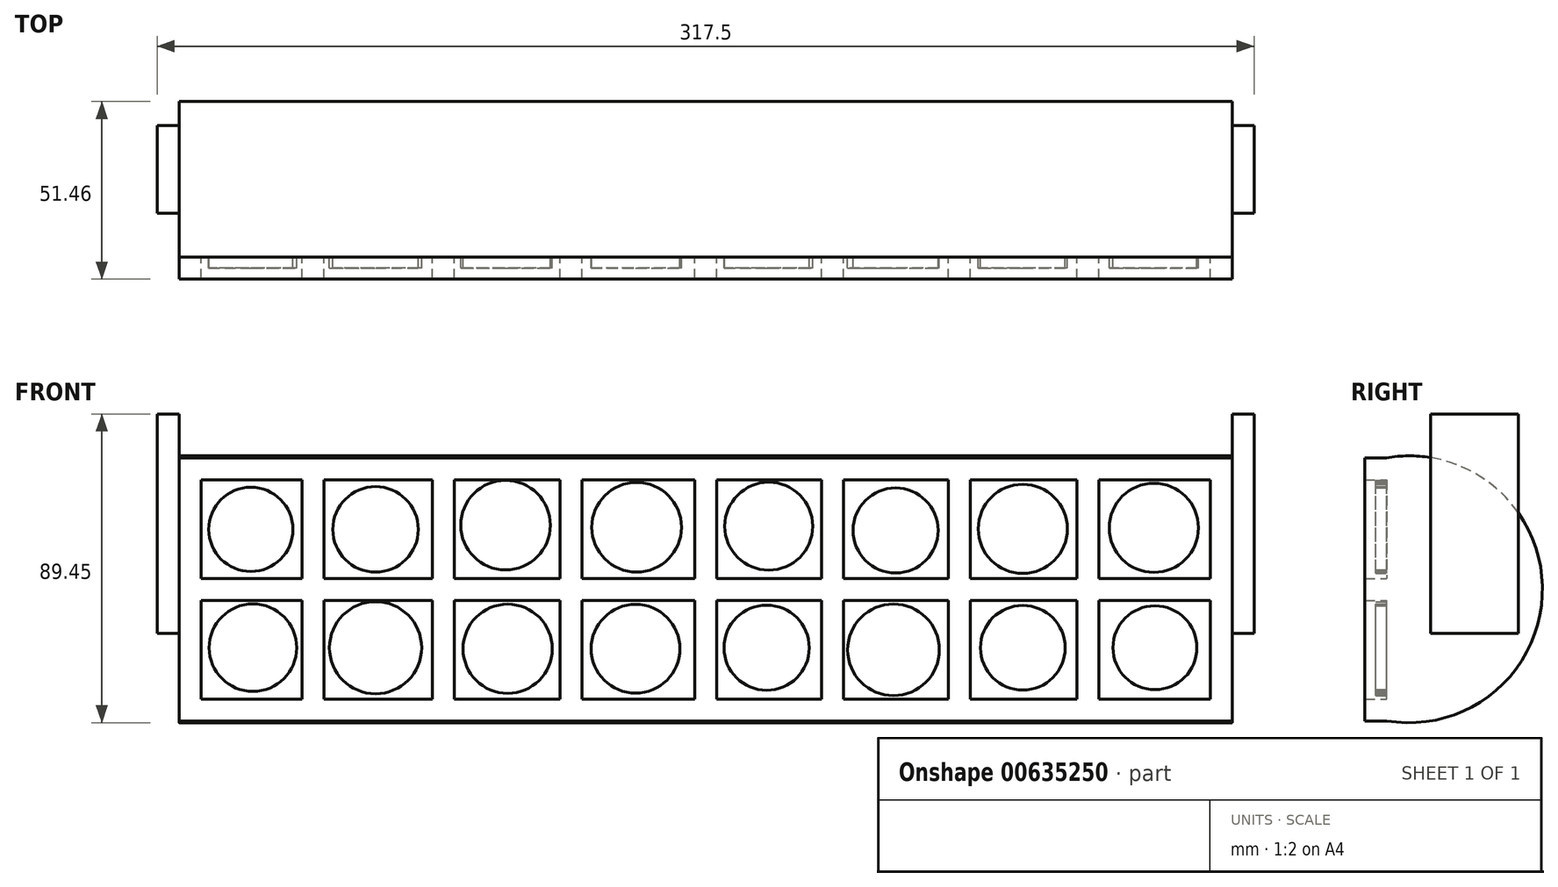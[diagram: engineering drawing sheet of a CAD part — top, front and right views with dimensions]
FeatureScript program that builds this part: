
annotation { "Feature Type Name" : "Feature", "Feature Type Description" : "" }
export const myFeature = defineFeature(function(context is Context, id is Id, definition is map)
    precondition{}
    {
        {
            var Q0;
            Q0=qCreatedBy(makeId("Right.planeOp"),FACE);
            var sketch = newSketch(context, id + "F0", { "sketchPlane" : qUnion([Q0])});
            skLineSegment(sketch, "E0", {"start": v(0, 0) * mm, "end": v(0, 76.2) * mm});
            skArc(sketch, "E1", {"start": v(0, 0) * mm, "mid": v(45.11, 38.1) * mm, "end": v(0, 76.2) * mm});
            skSolve(sketch);
        }
        {
            var Q0;
            Q0 = qSketchRegion(id + "F0", true);
            extrude(context, id + "F1", {"entities" : qUnion([Q0]), "depth" : 304.8 * mm, "offsetDistance" : 25.4 * mm});
        }
        {
            var Q0;
            Q0=makeQuery(id+"F1.opExtrude","CAP_FACE",FACE,{"disambiguationData":[OSD([sQuery(id+"F0.wireOp",EDGE,"E0"),sQuery(id+"F0.wireOp",EDGE,"E1")])],"isStart":true});
            var sketch = newSketch(context, id + "F2", { "sketchPlane" : qUnion([Q0])});
            skLineSegment(sketch, "E2.bottom", {"start": v(-38.1, 25.4) * mm, "end": v(-12.7, 25.4) * mm});
            skLineSegment(sketch, "E2.top", {"start": v(-38.1, 88.9) * mm, "end": v(-12.7, 88.9) * mm});
            skLineSegment(sketch, "E2.left", {"start": v(-38.1, 25.4) * mm, "end": v(-38.1, 88.9) * mm});
            skLineSegment(sketch, "E2.right", {"start": v(-12.7, 25.4) * mm, "end": v(-12.7, 88.9) * mm});
            skSolve(sketch);
        }
        {
            var Q0;
            Q0 = qSketchRegion(id + "F2", true);
            extrude(context, id + "F3", {"entities" : qUnion([Q0]), "operationType" : NewBodyOperationType.ADD, "depth" : 6.35 * mm, "offsetDistance" : 25.4 * mm});
        }
        {
            var Q0;
            Q0=makeQuery(id+"F1.opExtrude","CAP_FACE",FACE,{"disambiguationData":[OSD([sQuery(id+"F0.wireOp",EDGE,"E0"),sQuery(id+"F0.wireOp",EDGE,"E1")])],"isStart":false});
            var sketch = newSketch(context, id + "F4", { "sketchPlane" : qUnion([Q0])});
            skLineSegment(sketch, "E3.bottom", {"start": v(12.7, 25.4) * mm, "end": v(38.1, 25.4) * mm});
            skLineSegment(sketch, "E3.top", {"start": v(12.7, 88.9) * mm, "end": v(38.1, 88.9) * mm});
            skLineSegment(sketch, "E3.left", {"start": v(12.7, 25.4) * mm, "end": v(12.7, 88.9) * mm});
            skLineSegment(sketch, "E3.right", {"start": v(38.1, 25.4) * mm, "end": v(38.1, 88.9) * mm});
            skSolve(sketch);
        }
        {
            var Q0;
            Q0 = qSketchRegion(id + "F4", true);
            extrude(context, id + "F5", {"entities" : qUnion([Q0]), "operationType" : NewBodyOperationType.ADD, "depth" : 6.35 * mm, "offsetDistance" : 25.4 * mm});
        }
        {
            var Q0;
            Q0=makeQuery(id+"F1.opExtrude","SWEPT_FACE",FACE,{"disambiguationData":[OSD([sQuery(id+"F0.wireOp",EDGE,"E0")])]});
            var sketch = newSketch(context, id + "F6", { "sketchPlane" : qUnion([Q0])});
            skLineSegment(sketch, "E4.0", {"start": v(298.45, 69.85) * mm, "end": v(6.35, 69.85) * mm});
            skLineSegment(sketch, "E4.1", {"start": v(298.45, 6.35) * mm, "end": v(298.45, 69.85) * mm});
            skLineSegment(sketch, "E4.2", {"start": v(298.45, 6.35) * mm, "end": v(6.35, 6.35) * mm});
            skLineSegment(sketch, "E4.3", {"start": v(6.35, 6.35) * mm, "end": v(6.35, 69.85) * mm});
            skSolve(sketch);
        }
        {
            var Q0;
            Q0=makeQuery(id+"F6.imprint","IMPRINT",FACE,{"disambiguationData":[TD([[makeQuery(id+"F6.imprint","IMPRINT",EDGE,{"derivedFrom":sQuery(id+"F6.wireOp",EDGE,"E4.0")}),-1.0]])]});
            extrude(context, id + "F7", {"entities" : qUnion([Q0]), "operationType" : NewBodyOperationType.ADD, "depth" : 6.35 * mm, "offsetDistance" : 25.4 * mm});
        }
        {
            var Q0;
            Q0=makeQuery(id+"F1.opExtrude","SWEPT_FACE",FACE,{"disambiguationData":[OSD([sQuery(id+"F0.wireOp",EDGE,"E0")])]});
            var sketch = newSketch(context, id + "F8", { "sketchPlane" : qUnion([Q0])});
            skLineSegment(sketch, "E5.top", {"start": v(298.45, 41.27) * mm, "end": v(266.24, 41.27) * mm});
            skLineSegment(sketch, "E5.left", {"start": v(298.45, 34.92) * mm, "end": v(298.45, 41.27) * mm});
            skLineSegment(sketch, "E5.right", {"start": v(6.35, 34.92) * mm, "end": v(6.35, 41.27) * mm});
            skPoint(sketch, "E5.middle", {"position": v(152.4, 38.1) * mm});
            skPoint(sketch, "E5.middle.positionSnap0", {"position": v(6.35, 38.1) * mm});
            skPoint(sketch, "E5.middle.positionSnap1", {"position": v(152.4, 6.35) * mm});
            skPoint(sketch, "E5.centerSnap0", {"position": v(6.35, 38.1) * mm});
            skPoint(sketch, "E5.centerSnap1", {"position": v(152.4, 6.35) * mm});
            skLineSegment(sketch, "E6.bottom", {"start": v(149.23, 69.85) * mm, "end": v(155.58, 69.85) * mm});
            skLineSegment(sketch, "E6.top", {"start": v(149.23, 6.35) * mm, "end": v(155.58, 6.35) * mm});
            skLineSegment(sketch, "E6.left", {"start": v(149.23, 69.85) * mm, "end": v(149.23, 41.27) * mm});
            skLineSegment(sketch, "E6.right", {"start": v(155.58, 69.85) * mm, "end": v(155.58, 41.27) * mm});
            skLineSegment(sketch, "E7.bottom", {"start": v(79.62, 69.85) * mm, "end": v(73.27, 69.85) * mm});
            skLineSegment(sketch, "E7.top", {"start": v(79.62, 6.35) * mm, "end": v(73.27, 6.35) * mm});
            skLineSegment(sketch, "E7.left", {"start": v(79.62, 69.85) * mm, "end": v(79.62, 41.27) * mm});
            skLineSegment(sketch, "E7.right", {"start": v(73.27, 69.85) * mm, "end": v(73.27, 41.27) * mm});
            skPoint(sketch, "E7.middle", {"position": v(76.45, 38.1) * mm});
            skLineSegment(sketch, "E8.bottom", {"start": v(41.91, 69.85) * mm, "end": v(35.56, 69.85) * mm});
            skLineSegment(sketch, "E8.top", {"start": v(41.91, 6.35) * mm, "end": v(35.56, 6.35) * mm});
            skLineSegment(sketch, "E8.left", {"start": v(41.91, 69.85) * mm, "end": v(41.91, 41.27) * mm});
            skLineSegment(sketch, "E8.right", {"start": v(35.56, 69.85) * mm, "end": v(35.56, 41.27) * mm});
            skPoint(sketch, "E8.middle", {"position": v(38.74, 38.1) * mm});
            skLineSegment(sketch, "E9.bottom", {"start": v(116.59, 69.85) * mm, "end": v(110.24, 69.85) * mm});
            skLineSegment(sketch, "E9.top", {"start": v(116.59, 6.35) * mm, "end": v(110.24, 6.35) * mm});
            skLineSegment(sketch, "E9.left", {"start": v(116.59, 69.85) * mm, "end": v(116.59, 41.27) * mm});
            skLineSegment(sketch, "E9.right", {"start": v(110.24, 69.85) * mm, "end": v(110.24, 41.27) * mm});
            skPoint(sketch, "E9.middle", {"position": v(113.41, 38.1) * mm});
            skLineSegment(sketch, "E10.bottom", {"start": v(229.02, 69.85) * mm, "end": v(222.67, 69.85) * mm});
            skLineSegment(sketch, "E10.top", {"start": v(229.02, 6.35) * mm, "end": v(222.67, 6.35) * mm});
            skLineSegment(sketch, "E10.left", {"start": v(229.02, 69.85) * mm, "end": v(229.02, 41.27) * mm});
            skLineSegment(sketch, "E10.right", {"start": v(222.67, 69.85) * mm, "end": v(222.67, 41.27) * mm});
            skPoint(sketch, "E10.middle", {"position": v(225.85, 38.1) * mm});
            skLineSegment(sketch, "E11.bottom", {"start": v(192.37, 69.85) * mm, "end": v(186.02, 69.85) * mm});
            skLineSegment(sketch, "E11.top", {"start": v(192.37, 6.35) * mm, "end": v(186.02, 6.35) * mm});
            skLineSegment(sketch, "E11.left", {"start": v(192.37, 69.85) * mm, "end": v(192.37, 41.27) * mm});
            skLineSegment(sketch, "E11.right", {"start": v(186.02, 69.85) * mm, "end": v(186.02, 41.27) * mm});
            skPoint(sketch, "E11.middle", {"position": v(189.2, 38.1) * mm});
            skLineSegment(sketch, "E12.bottom", {"start": v(266.24, 69.85) * mm, "end": v(259.9, 69.85) * mm});
            skLineSegment(sketch, "E12.top", {"start": v(266.24, 6.35) * mm, "end": v(259.9, 6.35) * mm});
            skLineSegment(sketch, "E12.right", {"start": v(259.9, 69.85) * mm, "end": v(259.9, 41.27) * mm});
            skPoint(sketch, "E12.middle", {"position": v(263.07, 38.1) * mm});
            skLineSegment(sketch, "E13.trimOffspring", {"start": v(35.56, 41.27) * mm, "end": v(6.35, 41.27) * mm});
            skLineSegment(sketch, "E14.trimOffspring", {"start": v(35.56, 34.92) * mm, "end": v(6.35, 34.92) * mm});
            skLineSegment(sketch, "E15.trimOffspring", {"start": v(35.56, 34.92) * mm, "end": v(35.56, 6.35) * mm});
            skLineSegment(sketch, "E16.trimOffspring", {"start": v(41.91, 34.92) * mm, "end": v(41.91, 6.35) * mm});
            skLineSegment(sketch, "E17.trimOffspring", {"start": v(73.27, 41.27) * mm, "end": v(41.91, 41.27) * mm});
            skLineSegment(sketch, "E18.trimOffspring", {"start": v(73.27, 34.92) * mm, "end": v(73.27, 6.35) * mm});
            skLineSegment(sketch, "E19.trimOffspring", {"start": v(79.62, 34.92) * mm, "end": v(79.62, 6.35) * mm});
            skLineSegment(sketch, "E20.trimOffspring", {"start": v(73.27, 34.92) * mm, "end": v(41.91, 34.92) * mm});
            skLineSegment(sketch, "E21.trimOffspring", {"start": v(110.24, 41.27) * mm, "end": v(79.62, 41.27) * mm});
            skLineSegment(sketch, "E22.trimOffspring", {"start": v(110.24, 34.92) * mm, "end": v(110.24, 6.35) * mm});
            skLineSegment(sketch, "E23.trimOffspring", {"start": v(110.24, 34.92) * mm, "end": v(79.62, 34.92) * mm});
            skLineSegment(sketch, "E24.trimOffspring", {"start": v(116.59, 34.92) * mm, "end": v(116.59, 6.35) * mm});
            skLineSegment(sketch, "E25.trimOffspring", {"start": v(149.23, 41.27) * mm, "end": v(116.59, 41.27) * mm});
            skLineSegment(sketch, "E26.trimOffspring", {"start": v(155.58, 34.92) * mm, "end": v(155.58, 6.35) * mm});
            skLineSegment(sketch, "E27.trimOffspring", {"start": v(149.23, 34.92) * mm, "end": v(116.59, 34.92) * mm});
            skLineSegment(sketch, "E28.trimOffspring", {"start": v(149.23, 34.92) * mm, "end": v(149.23, 6.35) * mm});
            skLineSegment(sketch, "E29.trimOffspring", {"start": v(186.02, 41.27) * mm, "end": v(155.58, 41.27) * mm});
            skLineSegment(sketch, "E30.trimOffspring", {"start": v(186.02, 34.92) * mm, "end": v(186.02, 6.35) * mm});
            skLineSegment(sketch, "E31.trimOffspring", {"start": v(186.02, 34.92) * mm, "end": v(155.58, 34.92) * mm});
            skLineSegment(sketch, "E32.trimOffspring", {"start": v(192.37, 34.92) * mm, "end": v(192.37, 6.35) * mm});
            skLineSegment(sketch, "E33.trimOffspring", {"start": v(222.67, 41.27) * mm, "end": v(192.37, 41.27) * mm});
            skLineSegment(sketch, "E34.trimOffspring", {"start": v(222.67, 34.92) * mm, "end": v(222.67, 6.35) * mm});
            skLineSegment(sketch, "E35.trimOffspring", {"start": v(222.67, 34.92) * mm, "end": v(192.37, 34.92) * mm});
            skLineSegment(sketch, "E36.trimOffspring", {"start": v(229.02, 34.92) * mm, "end": v(229.02, 6.35) * mm});
            skLineSegment(sketch, "E37.trimOffspring", {"start": v(259.9, 41.27) * mm, "end": v(229.02, 41.27) * mm});
            skLineSegment(sketch, "E38.trimOffspring", {"start": v(266.24, 34.92) * mm, "end": v(266.24, 6.35) * mm});
            skLineSegment(sketch, "E39.trimOffspring", {"start": v(259.9, 34.92) * mm, "end": v(229.02, 34.92) * mm});
            skLineSegment(sketch, "E40.trimOffspring", {"start": v(259.9, 34.92) * mm, "end": v(259.9, 6.35) * mm});
            skLineSegment(sketch, "E41", {"start": v(266.24, 34.92) * mm, "end": v(298.45, 34.92) * mm});
            skLineSegment(sketch, "E42", {"start": v(266.24, 69.85) * mm, "end": v(266.24, 41.27) * mm});
            skSolve(sketch);
        }
        {
            var Q0;
            Q0 = qSketchRegion(id + "F8", true);
            extrude(context, id + "F9", {"entities" : qUnion([Q0]), "operationType" : NewBodyOperationType.ADD, "depth" : 6.35 * mm, "offsetDistance" : 25.4 * mm});
        }
        {
            var Q0;
            Q0=makeQuery(id+"F9.boolean.opBoolean","SPLIT",FACE,{"disambiguationData":[TD([makeQuery(id+"F9.opExtrude","SWEPT_FACE",FACE,{"disambiguationData":[OSD([sQuery(id+"F8.wireOp",EDGE,"E8.right")])]})])],"derivedFrom":makeQuery(id+"F1.opExtrude","SWEPT_FACE",FACE,{"disambiguationData":[OSD([sQuery(id+"F0.wireOp",EDGE,"E0")])]})});
            var sketch = newSketch(context, id + "F10", { "sketchPlane" : qUnion([Q0])});
            skCircle(sketch, "E43", {"center": v(20.78, 55.45) * mm, "radius": 12.18 * mm});
            skCircle(sketch, "E44", {"center": v(56.88, 55.45) * mm, "radius": 12.38 * mm});
            skCircle(sketch, "E45", {"center": v(21.39, 21.18) * mm, "radius": 12.67 * mm});
            skCircle(sketch, "E46", {"center": v(56.88, 21.18) * mm, "radius": 13.34 * mm});
            skCircle(sketch, "E47", {"center": v(94.5, 56.67) * mm, "radius": 12.97 * mm});
            skCircle(sketch, "E48", {"center": v(95.12, 20.88) * mm, "radius": 12.91 * mm});
            skCircle(sketch, "E49", {"center": v(132.45, 56.06) * mm, "radius": 12.98 * mm});
            skCircle(sketch, "E50", {"center": v(132.14, 20.88) * mm, "radius": 12.85 * mm});
            skCircle(sketch, "E51", {"center": v(170.7, 56.37) * mm, "radius": 12.73 * mm});
            skCircle(sketch, "E52", {"center": v(170.08, 21.18) * mm, "radius": 12.33 * mm});
            skCircle(sketch, "E53", {"center": v(207.4, 55.14) * mm, "radius": 12.3 * mm});
            skCircle(sketch, "E54", {"center": v(206.8, 20.57) * mm, "radius": 13.27 * mm});
            skCircle(sketch, "E55", {"center": v(244.22, 55.6) * mm, "radius": 12.9 * mm});
            skCircle(sketch, "E56", {"center": v(244.22, 21.18) * mm, "radius": 12.26 * mm});
            skCircle(sketch, "E57", {"center": v(282.16, 55.9) * mm, "radius": 12.91 * mm});
            skCircle(sketch, "E58", {"center": v(282.46, 21.18) * mm, "radius": 12.14 * mm});
            skSolve(sketch);
        }
        {
            var Q0;
            Q0 = qSketchRegion(id + "F10", true);
            extrude(context, id + "F11", {"entities" : qUnion([Q0]), "operationType" : NewBodyOperationType.ADD, "depth" : 3.17 * mm, "offsetDistance" : 25.4 * mm});
        }
    });
